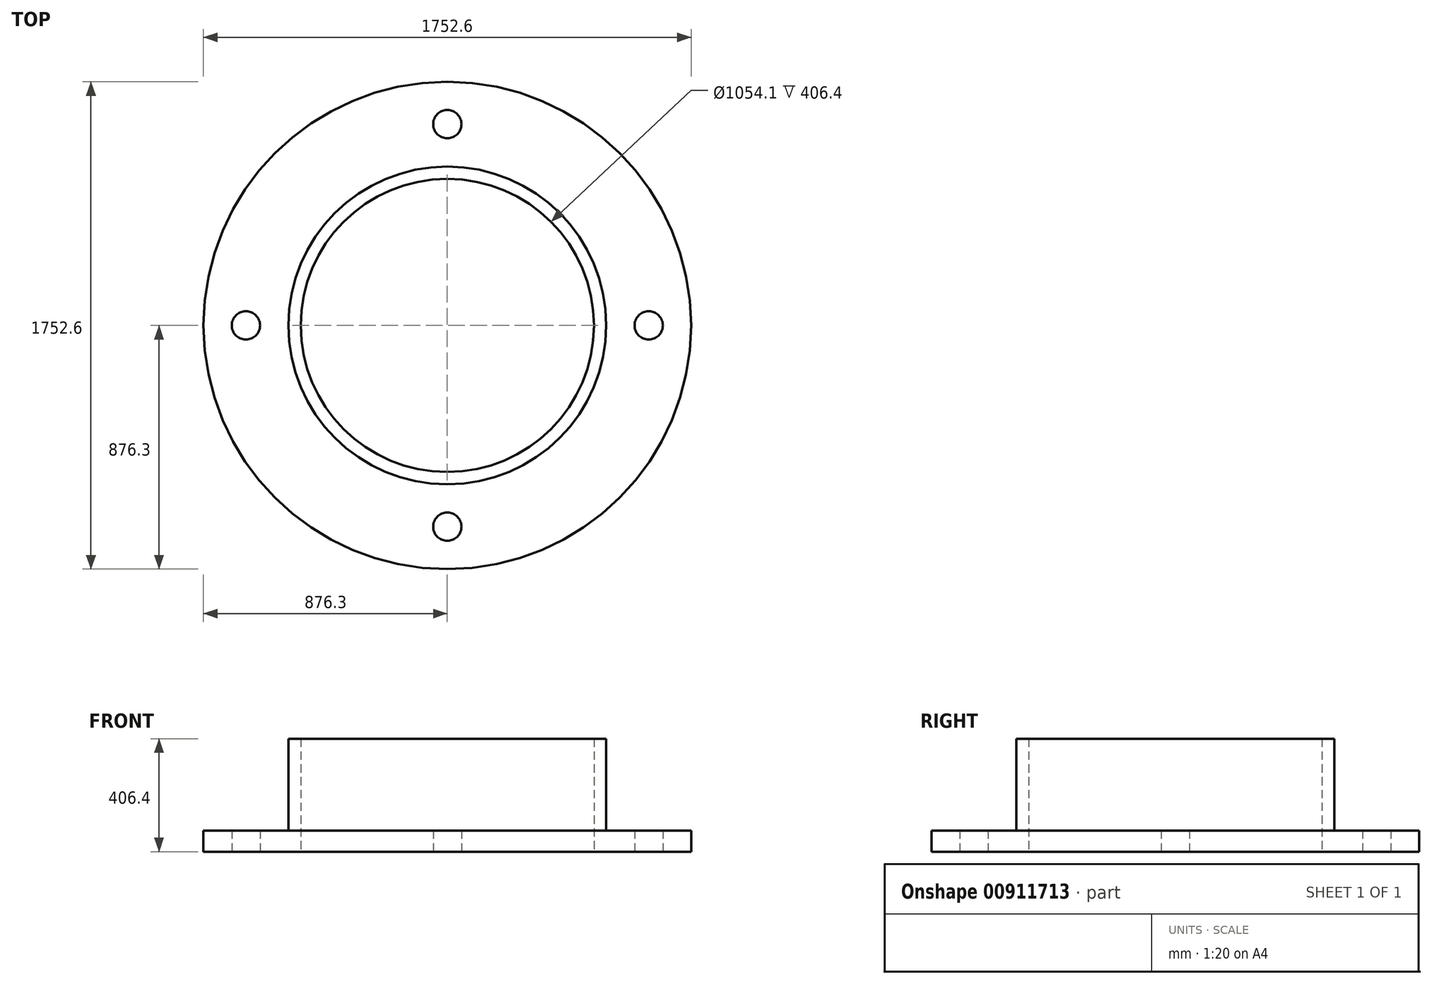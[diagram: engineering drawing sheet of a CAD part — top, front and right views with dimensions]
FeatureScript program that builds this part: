
annotation { "Feature Type Name" : "Feature", "Feature Type Description" : "" }
export const myFeature = defineFeature(function(context is Context, id is Id, definition is map)
    precondition{}
    {
        {
            var Q0;
            Q0=qCreatedBy(makeId("Top.planeOp"),FACE);
            var sketch = newSketch(context, id + "F0", { "sketchPlane" : qUnion([Q0])});
            skPoint(sketch, "E0.middle", {"position": v(0, 0) * mm});
            skCircle(sketch, "E1", {"center": v(0, 0) * mm, "radius": 527.05 * mm});
            skCircle(sketch, "E2", {"center": v(0, 0) * mm, "radius": 571.5 * mm});
            skCircle(sketch, "E3", {"center": v(0, 0) * mm, "radius": 876.3 * mm});
            skCircle(sketch, "E4", {"center": v(0, 723.9) * mm, "radius": 50.8 * mm});
            skCircle(sketch, "E5.1.0", {"center": v(-723.9, 0) * mm, "radius": 50.8 * mm});
            skCircle(sketch, "E5.2.0", {"center": v(0, -723.9) * mm, "radius": 50.8 * mm});
            skCircle(sketch, "E5.3.0", {"center": v(723.9, 0) * mm, "radius": 50.8 * mm});
            skSolve(sketch);
        }
        {
            var Q0;
            {var subQ7=sQuery(id+"F0.wireOp",EDGE,"E0.left");var subQ8=sQuery(id+"F0.wireOp",EDGE,"E0.top");var subQ9=makeQuery(id+"F0.imprint","INTERSECT",VERTEX,{"derivedFrom":[subQ8,subQ7]});Q0=makeQuery(id+"F0.imprint","IMPRINT",FACE,{"disambiguationData":[TD([[makeQuery(id+"F0.imprint","IMPRINT",EDGE,{"disambiguationData":[TD([[subQ9,-1.0]])],"derivedFrom":subQ8}),1.0]])]});}
            var Q1;
            {var subQ0=sQuery(id+"F0.wireOp",EDGE,"bJPlWt6Q-fWFR-6q8K-e8lr-7XfZDWMV1iGK.left");var subQ1=sQuery(id+"F0.wireOp",EDGE,"E0.bottom");var subQ2=makeQuery(id+"F0.imprint","INTERSECT",VERTEX,{"derivedFrom":[subQ1,subQ0]});Q1=makeQuery(id+"F0.imprint","IMPRINT",FACE,{"disambiguationData":[TD([[makeQuery(id+"F0.imprint","IMPRINT",EDGE,{"disambiguationData":[TD([[subQ2,-1.0]])],"derivedFrom":subQ1}),1.0]])]});}
            var Q2;
            {var subQ7=sQuery(id+"F0.wireOp",EDGE,"E0.bottom");var subQ9=sQuery(id+"F0.wireOp",EDGE,"E0.left");var subQ10=makeQuery(id+"F0.imprint","INTERSECT",VERTEX,{"derivedFrom":[subQ7,subQ9]});Q2=makeQuery(id+"F0.imprint","IMPRINT",FACE,{"disambiguationData":[TD([[makeQuery(id+"F0.imprint","IMPRINT",EDGE,{"disambiguationData":[TD([[subQ10,-1.0]])],"derivedFrom":subQ7}),-1.0]])]});}
            var Q3;
            {var subQ0=sQuery(id+"F0.wireOp",EDGE,"bJPlWt6Q-fWFR-6q8K-e8lr-7XfZDWMV1iGK.left");var subQ1=sQuery(id+"F0.wireOp",EDGE,"E0.top");var subQ2=makeQuery(id+"F0.imprint","INTERSECT",VERTEX,{"derivedFrom":[subQ1,subQ0]});Q3=makeQuery(id+"F0.imprint","IMPRINT",FACE,{"disambiguationData":[TD([[makeQuery(id+"F0.imprint","IMPRINT",EDGE,{"disambiguationData":[TD([[subQ2,-1.0]])],"derivedFrom":subQ1}),1.0]])]});}
            var Q4;
            {var subQ0=sQuery(id+"F0.wireOp",EDGE,"bJPlWt6Q-fWFR-6q8K-e8lr-7XfZDWMV1iGK.left");var subQ1=sQuery(id+"F0.wireOp",EDGE,"E0.top");var subQ2=makeQuery(id+"F0.imprint","INTERSECT",VERTEX,{"derivedFrom":[subQ1,subQ0]});Q4=makeQuery(id+"F0.imprint","IMPRINT",FACE,{"disambiguationData":[TD([[makeQuery(id+"F0.imprint","IMPRINT",EDGE,{"disambiguationData":[TD([[subQ2,-1.0]])],"derivedFrom":subQ1}),-1.0]])]});}
            var Q5;
            {var subQ0=sQuery(id+"F0.wireOp",EDGE,"bJPlWt6Q-fWFR-6q8K-e8lr-7XfZDWMV1iGK.left");var subQ1=sQuery(id+"F0.wireOp",EDGE,"E0.bottom");var subQ2=makeQuery(id+"F0.imprint","INTERSECT",VERTEX,{"derivedFrom":[subQ1,subQ0]});Q5=makeQuery(id+"F0.imprint","IMPRINT",FACE,{"disambiguationData":[TD([[makeQuery(id+"F0.imprint","IMPRINT",EDGE,{"disambiguationData":[TD([[subQ2,-1.0]])],"derivedFrom":subQ1}),-1.0]])]});}
            var Q6;
            {var subQ1=sQuery(id+"F0.wireOp",EDGE,"bJPlWt6Q-fWFR-6q8K-e8lr-7XfZDWMV1iGK.bottom");Q6=makeQuery(id+"F0.imprint","IMPRINT",FACE,{"disambiguationData":[TD([[makeQuery(id+"F0.imprint","IMPRINT",EDGE,{"derivedFrom":subQ1}),1.0]])]});}
            var Q7;
            {var subQ0=sQuery(id+"F0.wireOp",EDGE,"uCDm0gm9-0pKr-2IA7-bEzO-ZyxMw17Tw9Nd.bottom");var subQ1=sQuery(id+"F0.wireOp",EDGE,"ElkeHvbq-XJBf-Tpza-nRTL-gXQnVyS3yxsv.left");var subQ2=makeQuery(id+"F0.imprint","INTERSECT",VERTEX,{"derivedFrom":[subQ1,subQ0]});Q7=makeQuery(id+"F0.imprint","IMPRINT",FACE,{"disambiguationData":[TD([[makeQuery(id+"F0.imprint","IMPRINT",EDGE,{"disambiguationData":[TD([[subQ2,-1.0]])],"derivedFrom":subQ1}),1.0]])]});}
            var Q8;
            {var subQ0=sQuery(id+"F0.wireOp",EDGE,"bJPlWt6Q-fWFR-6q8K-e8lr-7XfZDWMV1iGK.right");var subQ1=sQuery(id+"F0.wireOp",EDGE,"E1");var subQ2=makeQuery(id+"F0.imprint","INTERSECT",VERTEX,{"disambiguationData":[OD(1.0)],"derivedFrom":[subQ1,subQ0]});Q8=makeQuery(id+"F0.imprint","IMPRINT",FACE,{"disambiguationData":[TD([[makeQuery(id+"F0.imprint","IMPRINT",EDGE,{"disambiguationData":[TD([[subQ2,-1.0]])],"derivedFrom":subQ1}),-1.0]])]});}
            var Q9;
            {var subQ0=sQuery(id+"F0.wireOp",EDGE,"E0.left");var subQ1=sQuery(id+"F0.wireOp",EDGE,"E0.bottom");var subQ2=makeQuery(id+"F0.imprint","INTERSECT",VERTEX,{"derivedFrom":[subQ1,subQ0]});Q9=makeQuery(id+"F0.imprint","IMPRINT",FACE,{"disambiguationData":[TD([[makeQuery(id+"F0.imprint","IMPRINT",EDGE,{"disambiguationData":[TD([[subQ2,-1.0]])],"derivedFrom":subQ1}),1.0]])]});}
            var Q10;
            {var subQ0=sQuery(id+"F0.wireOp",EDGE,"E0.right");var subQ1=sQuery(id+"F0.wireOp",EDGE,"E0.bottom");var subQ2=makeQuery(id+"F0.imprint","INTERSECT",VERTEX,{"derivedFrom":[subQ1,subQ0]});Q10=makeQuery(id+"F0.imprint","IMPRINT",FACE,{"disambiguationData":[TD([[makeQuery(id+"F0.imprint","IMPRINT",EDGE,{"disambiguationData":[TD([[subQ2,1.0]])],"derivedFrom":subQ1}),1.0]])]});}
            var Q11;
            {var subQ7=sQuery(id+"F0.wireOp",EDGE,"E0.right");var subQ8=sQuery(id+"F0.wireOp",EDGE,"E0.top");var subQ9=makeQuery(id+"F0.imprint","INTERSECT",VERTEX,{"derivedFrom":[subQ8,subQ7]});Q11=makeQuery(id+"F0.imprint","IMPRINT",FACE,{"disambiguationData":[TD([[makeQuery(id+"F0.imprint","IMPRINT",EDGE,{"disambiguationData":[TD([[subQ9,1.0]])],"derivedFrom":subQ8}),1.0]])]});}
            var Q12;
            {var subQ0=sQuery(id+"F0.wireOp",EDGE,"uCDm0gm9-0pKr-2IA7-bEzO-ZyxMw17Tw9Nd.top");var subQ1=sQuery(id+"F0.wireOp",EDGE,"E1");var subQ2=makeQuery(id+"F0.imprint","INTERSECT",VERTEX,{"disambiguationData":[OD(0.0)],"derivedFrom":[subQ1,subQ0]});Q12=makeQuery(id+"F0.imprint","IMPRINT",FACE,{"disambiguationData":[TD([[makeQuery(id+"F0.imprint","IMPRINT",EDGE,{"disambiguationData":[TD([[subQ2,1.0]])],"derivedFrom":subQ1}),-1.0]])]});}
            var Q13;
            {var subQ1=sQuery(id+"F0.wireOp",EDGE,"ElkeHvbq-XJBf-Tpza-nRTL-gXQnVyS3yxsv.bottom");var subQ7=sQuery(id+"F0.wireOp",EDGE,"ElkeHvbq-XJBf-Tpza-nRTL-gXQnVyS3yxsv.right");var subQ9=makeQuery(id+"F0.imprint","INTERSECT",VERTEX,{"derivedFrom":[subQ1,subQ7]});Q13=makeQuery(id+"F0.imprint","IMPRINT",FACE,{"disambiguationData":[TD([[makeQuery(id+"F0.imprint","IMPRINT",EDGE,{"disambiguationData":[TD([[subQ9,1.0]])],"derivedFrom":subQ1}),-1.0]])]});}
            var Q14;
            {var subQ0=sQuery(id+"F0.wireOp",EDGE,"uCDm0gm9-0pKr-2IA7-bEzO-ZyxMw17Tw9Nd.bottom");var subQ1=sQuery(id+"F0.wireOp",EDGE,"E0.left");var subQ2=makeQuery(id+"F0.imprint","INTERSECT",VERTEX,{"derivedFrom":[subQ1,subQ0]});Q14=makeQuery(id+"F0.imprint","IMPRINT",FACE,{"disambiguationData":[TD([[makeQuery(id+"F0.imprint","IMPRINT",EDGE,{"disambiguationData":[TD([[subQ2,-1.0]])],"derivedFrom":subQ1}),1.0]])]});}
            var Q15;
            {var subQ0=sQuery(id+"F0.wireOp",EDGE,"E0.right");var subQ1=sQuery(id+"F0.wireOp",EDGE,"E0.top");var subQ2=makeQuery(id+"F0.imprint","INTERSECT",VERTEX,{"derivedFrom":[subQ1,subQ0]});Q15=makeQuery(id+"F0.imprint","IMPRINT",FACE,{"disambiguationData":[TD([[makeQuery(id+"F0.imprint","IMPRINT",EDGE,{"disambiguationData":[TD([[subQ2,1.0]])],"derivedFrom":subQ1}),-1.0]])]});}
            var Q16;
            {var subQ0=sQuery(id+"F0.wireOp",EDGE,"uCDm0gm9-0pKr-2IA7-bEzO-ZyxMw17Tw9Nd.bottom");var subQ1=sQuery(id+"F0.wireOp",EDGE,"E0.right");var subQ2=makeQuery(id+"F0.imprint","INTERSECT",VERTEX,{"derivedFrom":[subQ1,subQ0]});Q16=makeQuery(id+"F0.imprint","IMPRINT",FACE,{"disambiguationData":[TD([[makeQuery(id+"F0.imprint","IMPRINT",EDGE,{"disambiguationData":[TD([[subQ2,-1.0]])],"derivedFrom":subQ1}),-1.0]])]});}
            var Q17;
            {var subQ0=sQuery(id+"F0.wireOp",EDGE,"bJPlWt6Q-fWFR-6q8K-e8lr-7XfZDWMV1iGK.left");var subQ1=sQuery(id+"F0.wireOp",EDGE,"E1");var subQ2=makeQuery(id+"F0.imprint","INTERSECT",VERTEX,{"disambiguationData":[OD(1.0)],"derivedFrom":[subQ1,subQ0]});Q17=makeQuery(id+"F0.imprint","IMPRINT",FACE,{"disambiguationData":[TD([[makeQuery(id+"F0.imprint","IMPRINT",EDGE,{"disambiguationData":[TD([[subQ2,-1.0]])],"derivedFrom":subQ1}),-1.0]])]});}
            var Q18;
            {var subQ1=sQuery(id+"F0.wireOp",EDGE,"ElkeHvbq-XJBf-Tpza-nRTL-gXQnVyS3yxsv.top");var subQ5=sQuery(id+"F0.wireOp",EDGE,"ElkeHvbq-XJBf-Tpza-nRTL-gXQnVyS3yxsv.right");var subQ6=makeQuery(id+"F0.imprint","INTERSECT",VERTEX,{"derivedFrom":[subQ1,subQ5]});Q18=makeQuery(id+"F0.imprint","IMPRINT",FACE,{"disambiguationData":[TD([[makeQuery(id+"F0.imprint","IMPRINT",EDGE,{"disambiguationData":[TD([[subQ6,1.0]])],"derivedFrom":subQ1}),1.0]])]});}
            var Q19;
            {var subQ0=sQuery(id+"F0.wireOp",EDGE,"uCDm0gm9-0pKr-2IA7-bEzO-ZyxMw17Tw9Nd.top");var subQ1=sQuery(id+"F0.wireOp",EDGE,"E1");var subQ2=makeQuery(id+"F0.imprint","INTERSECT",VERTEX,{"disambiguationData":[OD(1.0)],"derivedFrom":[subQ1,subQ0]});Q19=makeQuery(id+"F0.imprint","IMPRINT",FACE,{"disambiguationData":[TD([[makeQuery(id+"F0.imprint","IMPRINT",EDGE,{"disambiguationData":[TD([[subQ2,-1.0]])],"derivedFrom":subQ1}),-1.0]])]});}
            var Q20;
            {var subQ0=sQuery(id+"F0.wireOp",EDGE,"uCDm0gm9-0pKr-2IA7-bEzO-ZyxMw17Tw9Nd.bottom");var subQ1=sQuery(id+"F0.wireOp",EDGE,"ElkeHvbq-XJBf-Tpza-nRTL-gXQnVyS3yxsv.right");var subQ2=makeQuery(id+"F0.imprint","INTERSECT",VERTEX,{"derivedFrom":[subQ1,subQ0]});Q20=makeQuery(id+"F0.imprint","IMPRINT",FACE,{"disambiguationData":[TD([[makeQuery(id+"F0.imprint","IMPRINT",EDGE,{"disambiguationData":[TD([[subQ2,-1.0]])],"derivedFrom":subQ1}),-1.0]])]});}
            var Q21;
            {var subQ0=sQuery(id+"F0.wireOp",EDGE,"uCDm0gm9-0pKr-2IA7-bEzO-ZyxMw17Tw9Nd.right");Q21=makeQuery(id+"F0.imprint","IMPRINT",FACE,{"disambiguationData":[TD([[makeQuery(id+"F0.imprint","IMPRINT",EDGE,{"derivedFrom":subQ0}),1.0]])]});}
            var Q22;
            {var subQ0=sQuery(id+"F0.wireOp",EDGE,"E0.left");var subQ1=sQuery(id+"F0.wireOp",EDGE,"E0.top");var subQ2=makeQuery(id+"F0.imprint","INTERSECT",VERTEX,{"derivedFrom":[subQ1,subQ0]});Q22=makeQuery(id+"F0.imprint","IMPRINT",FACE,{"disambiguationData":[TD([[makeQuery(id+"F0.imprint","IMPRINT",EDGE,{"disambiguationData":[TD([[subQ2,-1.0]])],"derivedFrom":subQ1}),-1.0]])]});}
            var Q23;
            {var subQ0=sQuery(id+"F0.wireOp",EDGE,"uCDm0gm9-0pKr-2IA7-bEzO-ZyxMw17Tw9Nd.bottom");var subQ1=sQuery(id+"F0.wireOp",EDGE,"E0.right");var subQ2=makeQuery(id+"F0.imprint","INTERSECT",VERTEX,{"derivedFrom":[subQ1,subQ0]});Q23=makeQuery(id+"F0.imprint","IMPRINT",FACE,{"disambiguationData":[TD([[makeQuery(id+"F0.imprint","IMPRINT",EDGE,{"disambiguationData":[TD([[subQ2,-1.0]])],"derivedFrom":subQ1}),1.0]])]});}
            var Q24;
            {var subQ0=sQuery(id+"F0.wireOp",EDGE,"uCDm0gm9-0pKr-2IA7-bEzO-ZyxMw17Tw9Nd.bottom");var subQ1=sQuery(id+"F0.wireOp",EDGE,"E1");var subQ2=makeQuery(id+"F0.imprint","INTERSECT",VERTEX,{"disambiguationData":[OD(0.0)],"derivedFrom":[subQ1,subQ0]});Q24=makeQuery(id+"F0.imprint","IMPRINT",FACE,{"disambiguationData":[TD([[makeQuery(id+"F0.imprint","IMPRINT",EDGE,{"disambiguationData":[TD([[subQ2,-1.0]])],"derivedFrom":subQ1}),-1.0]])]});}
            var Q25;
            {var subQ0=sQuery(id+"F0.wireOp",EDGE,"uCDm0gm9-0pKr-2IA7-bEzO-ZyxMw17Tw9Nd.bottom");var subQ1=sQuery(id+"F0.wireOp",EDGE,"E0.left");var subQ2=makeQuery(id+"F0.imprint","INTERSECT",VERTEX,{"derivedFrom":[subQ1,subQ0]});Q25=makeQuery(id+"F0.imprint","IMPRINT",FACE,{"disambiguationData":[TD([[makeQuery(id+"F0.imprint","IMPRINT",EDGE,{"disambiguationData":[TD([[subQ2,-1.0]])],"derivedFrom":subQ1}),-1.0]])]});}
            var Q26;
            {var subQ0=sQuery(id+"F0.wireOp",EDGE,"bJPlWt6Q-fWFR-6q8K-e8lr-7XfZDWMV1iGK.left");var subQ1=sQuery(id+"F0.wireOp",EDGE,"ElkeHvbq-XJBf-Tpza-nRTL-gXQnVyS3yxsv.bottom");var subQ2=makeQuery(id+"F0.imprint","INTERSECT",VERTEX,{"derivedFrom":[subQ1,subQ0]});Q26=makeQuery(id+"F0.imprint","IMPRINT",FACE,{"disambiguationData":[TD([[makeQuery(id+"F0.imprint","IMPRINT",EDGE,{"disambiguationData":[TD([[subQ2,-1.0]])],"derivedFrom":subQ1}),-1.0]])]});}
            var Q27;
            {var subQ0=sQuery(id+"F0.wireOp",EDGE,"uCDm0gm9-0pKr-2IA7-bEzO-ZyxMw17Tw9Nd.left");Q27=makeQuery(id+"F0.imprint","IMPRINT",FACE,{"disambiguationData":[TD([[makeQuery(id+"F0.imprint","IMPRINT",EDGE,{"derivedFrom":subQ0}),-1.0]])]});}
            var Q28;
            {var subQ1=sQuery(id+"F0.wireOp",EDGE,"bJPlWt6Q-fWFR-6q8K-e8lr-7XfZDWMV1iGK.top");Q28=makeQuery(id+"F0.imprint","IMPRINT",FACE,{"disambiguationData":[TD([[makeQuery(id+"F0.imprint","IMPRINT",EDGE,{"derivedFrom":subQ1}),-1.0]])]});}
            var Q29;
            {var subQ0=sQuery(id+"F0.wireOp",EDGE,"bJPlWt6Q-fWFR-6q8K-e8lr-7XfZDWMV1iGK.left");var subQ1=sQuery(id+"F0.wireOp",EDGE,"ElkeHvbq-XJBf-Tpza-nRTL-gXQnVyS3yxsv.top");var subQ2=makeQuery(id+"F0.imprint","INTERSECT",VERTEX,{"derivedFrom":[subQ1,subQ0]});Q29=makeQuery(id+"F0.imprint","IMPRINT",FACE,{"disambiguationData":[TD([[makeQuery(id+"F0.imprint","IMPRINT",EDGE,{"disambiguationData":[TD([[subQ2,-1.0]])],"derivedFrom":subQ1}),1.0]])]});}
            var Q30;
            {var subQ0=sQuery(id+"F0.wireOp",EDGE,"bJPlWt6Q-fWFR-6q8K-e8lr-7XfZDWMV1iGK.right");var subQ1=sQuery(id+"F0.wireOp",EDGE,"E1");var subQ2=makeQuery(id+"F0.imprint","INTERSECT",VERTEX,{"disambiguationData":[OD(0.0)],"derivedFrom":[subQ1,subQ0]});Q30=makeQuery(id+"F0.imprint","IMPRINT",FACE,{"disambiguationData":[TD([[makeQuery(id+"F0.imprint","IMPRINT",EDGE,{"disambiguationData":[TD([[subQ2,-1.0]])],"derivedFrom":subQ1}),-1.0]])]});}
            var Q31;
            {var subQ0=sQuery(id+"F0.wireOp",EDGE,"bJPlWt6Q-fWFR-6q8K-e8lr-7XfZDWMV1iGK.right");var subQ1=sQuery(id+"F0.wireOp",EDGE,"E1");var subQ2=makeQuery(id+"F0.imprint","INTERSECT",VERTEX,{"disambiguationData":[OD(0.0)],"derivedFrom":[subQ1,subQ0]});Q31=makeQuery(id+"F0.imprint","IMPRINT",FACE,{"disambiguationData":[TD([[makeQuery(id+"F0.imprint","IMPRINT",EDGE,{"disambiguationData":[TD([[subQ2,1.0]])],"derivedFrom":subQ1}),-1.0]])]});}
            var Q32;
            {var subQ0=sQuery(id+"F0.wireOp",EDGE,"bJPlWt6Q-fWFR-6q8K-e8lr-7XfZDWMV1iGK.left");var subQ1=sQuery(id+"F0.wireOp",EDGE,"E1");var subQ2=makeQuery(id+"F0.imprint","INTERSECT",VERTEX,{"disambiguationData":[OD(0.0)],"derivedFrom":[subQ1,subQ0]});Q32=makeQuery(id+"F0.imprint","IMPRINT",FACE,{"disambiguationData":[TD([[makeQuery(id+"F0.imprint","IMPRINT",EDGE,{"disambiguationData":[TD([[subQ2,-1.0]])],"derivedFrom":subQ1}),-1.0]])]});}
            var Q33;
            {var subQ5=sQuery(id+"F0.wireOp",EDGE,"ElkeHvbq-XJBf-Tpza-nRTL-gXQnVyS3yxsv.left");var subQ6=sQuery(id+"F0.wireOp",EDGE,"ElkeHvbq-XJBf-Tpza-nRTL-gXQnVyS3yxsv.top");var subQ7=makeQuery(id+"F0.imprint","INTERSECT",VERTEX,{"derivedFrom":[subQ6,subQ5]});Q33=makeQuery(id+"F0.imprint","IMPRINT",FACE,{"disambiguationData":[TD([[makeQuery(id+"F0.imprint","IMPRINT",EDGE,{"disambiguationData":[TD([[subQ7,-1.0]])],"derivedFrom":subQ6}),1.0]])]});}
            var Q34;
            {var subQ1=sQuery(id+"F0.wireOp",EDGE,"ElkeHvbq-XJBf-Tpza-nRTL-gXQnVyS3yxsv.bottom");var subQ5=sQuery(id+"F0.wireOp",EDGE,"ElkeHvbq-XJBf-Tpza-nRTL-gXQnVyS3yxsv.right");var subQ6=makeQuery(id+"F0.imprint","INTERSECT",VERTEX,{"derivedFrom":[subQ1,subQ5]});Q34=makeQuery(id+"F0.imprint","IMPRINT",FACE,{"disambiguationData":[TD([[makeQuery(id+"F0.imprint","IMPRINT",EDGE,{"disambiguationData":[TD([[subQ6,1.0]])],"derivedFrom":subQ1}),1.0]])]});}
            var Q35;
            {var subQ1=sQuery(id+"F0.wireOp",EDGE,"E0.right");var subQ9=sQuery(id+"F0.wireOp",EDGE,"E0.bottom");var subQ11=makeQuery(id+"F0.imprint","INTERSECT",VERTEX,{"derivedFrom":[subQ9,subQ1]});Q35=makeQuery(id+"F0.imprint","IMPRINT",FACE,{"disambiguationData":[TD([[makeQuery(id+"F0.imprint","IMPRINT",EDGE,{"disambiguationData":[TD([[subQ11,1.0]])],"derivedFrom":subQ9}),-1.0]])]});}
            var Q36;
            {var subQ0=sQuery(id+"F0.wireOp",EDGE,"bJPlWt6Q-fWFR-6q8K-e8lr-7XfZDWMV1iGK.left");var subQ1=sQuery(id+"F0.wireOp",EDGE,"ElkeHvbq-XJBf-Tpza-nRTL-gXQnVyS3yxsv.bottom");var subQ2=makeQuery(id+"F0.imprint","INTERSECT",VERTEX,{"derivedFrom":[subQ1,subQ0]});Q36=makeQuery(id+"F0.imprint","IMPRINT",FACE,{"disambiguationData":[TD([[makeQuery(id+"F0.imprint","IMPRINT",EDGE,{"disambiguationData":[TD([[subQ2,-1.0]])],"derivedFrom":subQ1}),1.0]])]});}
            var Q37;
            {var subQ0=sQuery(id+"F0.wireOp",EDGE,"uCDm0gm9-0pKr-2IA7-bEzO-ZyxMw17Tw9Nd.bottom");var subQ1=sQuery(id+"F0.wireOp",EDGE,"ElkeHvbq-XJBf-Tpza-nRTL-gXQnVyS3yxsv.left");var subQ2=makeQuery(id+"F0.imprint","INTERSECT",VERTEX,{"derivedFrom":[subQ1,subQ0]});Q37=makeQuery(id+"F0.imprint","IMPRINT",FACE,{"disambiguationData":[TD([[makeQuery(id+"F0.imprint","IMPRINT",EDGE,{"disambiguationData":[TD([[subQ2,-1.0]])],"derivedFrom":subQ1}),-1.0]])]});}
            var Q38;
            {var subQ1=sQuery(id+"F0.wireOp",EDGE,"ElkeHvbq-XJBf-Tpza-nRTL-gXQnVyS3yxsv.left");var subQ5=sQuery(id+"F0.wireOp",EDGE,"ElkeHvbq-XJBf-Tpza-nRTL-gXQnVyS3yxsv.top");var subQ6=makeQuery(id+"F0.imprint","INTERSECT",VERTEX,{"derivedFrom":[subQ5,subQ1]});Q38=makeQuery(id+"F0.imprint","IMPRINT",FACE,{"disambiguationData":[TD([[makeQuery(id+"F0.imprint","IMPRINT",EDGE,{"disambiguationData":[TD([[subQ6,-1.0]])],"derivedFrom":subQ5}),-1.0]])]});}
            var Q39;
            {var subQ0=sQuery(id+"F0.wireOp",EDGE,"uCDm0gm9-0pKr-2IA7-bEzO-ZyxMw17Tw9Nd.bottom");var subQ1=sQuery(id+"F0.wireOp",EDGE,"ElkeHvbq-XJBf-Tpza-nRTL-gXQnVyS3yxsv.right");var subQ2=makeQuery(id+"F0.imprint","INTERSECT",VERTEX,{"derivedFrom":[subQ1,subQ0]});Q39=makeQuery(id+"F0.imprint","IMPRINT",FACE,{"disambiguationData":[TD([[makeQuery(id+"F0.imprint","IMPRINT",EDGE,{"disambiguationData":[TD([[subQ2,-1.0]])],"derivedFrom":subQ1}),1.0]])]});}
            var Q40;
            {var subQ1=sQuery(id+"F0.wireOp",EDGE,"ElkeHvbq-XJBf-Tpza-nRTL-gXQnVyS3yxsv.bottom");var subQ7=sQuery(id+"F0.wireOp",EDGE,"ElkeHvbq-XJBf-Tpza-nRTL-gXQnVyS3yxsv.left");var subQ9=makeQuery(id+"F0.imprint","INTERSECT",VERTEX,{"derivedFrom":[subQ1,subQ7]});Q40=makeQuery(id+"F0.imprint","IMPRINT",FACE,{"disambiguationData":[TD([[makeQuery(id+"F0.imprint","IMPRINT",EDGE,{"disambiguationData":[TD([[subQ9,-1.0]])],"derivedFrom":subQ1}),-1.0]])]});}
            var Q41;
            {var subQ0=sQuery(id+"F0.wireOp",EDGE,"bJPlWt6Q-fWFR-6q8K-e8lr-7XfZDWMV1iGK.left");var subQ1=sQuery(id+"F0.wireOp",EDGE,"ElkeHvbq-XJBf-Tpza-nRTL-gXQnVyS3yxsv.top");var subQ2=makeQuery(id+"F0.imprint","INTERSECT",VERTEX,{"derivedFrom":[subQ1,subQ0]});Q41=makeQuery(id+"F0.imprint","IMPRINT",FACE,{"disambiguationData":[TD([[makeQuery(id+"F0.imprint","IMPRINT",EDGE,{"disambiguationData":[TD([[subQ2,-1.0]])],"derivedFrom":subQ1}),-1.0]])]});}
            var Q42;
            {var subQ1=sQuery(id+"F0.wireOp",EDGE,"ElkeHvbq-XJBf-Tpza-nRTL-gXQnVyS3yxsv.bottom");var subQ5=sQuery(id+"F0.wireOp",EDGE,"ElkeHvbq-XJBf-Tpza-nRTL-gXQnVyS3yxsv.left");var subQ6=makeQuery(id+"F0.imprint","INTERSECT",VERTEX,{"derivedFrom":[subQ1,subQ5]});Q42=makeQuery(id+"F0.imprint","IMPRINT",FACE,{"disambiguationData":[TD([[makeQuery(id+"F0.imprint","IMPRINT",EDGE,{"disambiguationData":[TD([[subQ6,-1.0]])],"derivedFrom":subQ1}),1.0]])]});}
            var Q43;
            {var subQ1=sQuery(id+"F0.wireOp",EDGE,"ElkeHvbq-XJBf-Tpza-nRTL-gXQnVyS3yxsv.top");var subQ9=sQuery(id+"F0.wireOp",EDGE,"ElkeHvbq-XJBf-Tpza-nRTL-gXQnVyS3yxsv.right");var subQ10=makeQuery(id+"F0.imprint","INTERSECT",VERTEX,{"derivedFrom":[subQ1,subQ9]});Q43=makeQuery(id+"F0.imprint","IMPRINT",FACE,{"disambiguationData":[TD([[makeQuery(id+"F0.imprint","IMPRINT",EDGE,{"disambiguationData":[TD([[subQ10,1.0]])],"derivedFrom":subQ1}),-1.0]])]});}
            var Q44;
            Q44=makeQuery(id+"F0.imprint","IMPRINT",FACE,{"disambiguationData":[TD([[makeQuery(id+"F0.imprint","IMPRINT",EDGE,{"derivedFrom":sQuery(id+"F0.wireOp",EDGE,"fNri1SRu-FuhW-Q3Wo-20dk-0Yi258a3IsZ0")}),-1.0]])]});
            var Q45;
            {var subQ4=sQuery(id+"F0.wireOp",EDGE,"VQf29DOb-Ug8P-LxES-Ujji-pntrdd86x7RR.top");var subQ5=sQuery(id+"F0.wireOp",EDGE,"E2");var subQ6=makeQuery(id+"F0.imprint","INTERSECT",VERTEX,{"derivedFrom":[subQ5,subQ4]});Q45=makeQuery(id+"F0.imprint","IMPRINT",FACE,{"disambiguationData":[TD([[makeQuery(id+"F0.imprint","IMPRINT",EDGE,{"disambiguationData":[TD([[subQ6,-1.0]])],"derivedFrom":subQ5}),1.0]])]});}
            var Q46;
            Q46=makeQuery(id+"F0.imprint","IMPRINT",FACE,{"disambiguationData":[TD([[makeQuery(id+"F0.imprint","IMPRINT",EDGE,{"derivedFrom":sQuery(id+"F0.wireOp",EDGE,"70675ac1-52d6-47e0-aa64-0ae3552453f1.3.1")}),-1.0]])]});
            var Q47;
            {var subQ0=sQuery(id+"F0.wireOp",EDGE,"70675ac1-52d6-47e0-aa64-0ae3552453f1.3.2");var subQ6=sQuery(id+"F0.wireOp",EDGE,"E2");var subQ7=makeQuery(id+"F0.imprint","INTERSECT",VERTEX,{"derivedFrom":[subQ6,subQ0]});Q47=makeQuery(id+"F0.imprint","IMPRINT",FACE,{"disambiguationData":[TD([[makeQuery(id+"F0.imprint","IMPRINT",EDGE,{"disambiguationData":[TD([[subQ7,-1.0]])],"derivedFrom":subQ6}),1.0]])]});}
            var Q48;
            Q48=makeQuery(id+"F0.imprint","IMPRINT",FACE,{"disambiguationData":[TD([[makeQuery(id+"F0.imprint","IMPRINT",EDGE,{"derivedFrom":sQuery(id+"F0.wireOp",EDGE,"70675ac1-52d6-47e0-aa64-0ae3552453f1.2.1")}),-1.0]])]});
            var Q49;
            {var subQ3=sQuery(id+"F0.wireOp",EDGE,"E2");var subQ6=sQuery(id+"F0.wireOp",EDGE,"70675ac1-52d6-47e0-aa64-0ae3552453f1.2.4");var subQ8=makeQuery(id+"F0.imprint","INTERSECT",VERTEX,{"derivedFrom":[subQ3,subQ6]});Q49=makeQuery(id+"F0.imprint","IMPRINT",FACE,{"disambiguationData":[TD([[makeQuery(id+"F0.imprint","IMPRINT",EDGE,{"disambiguationData":[TD([[subQ8,1.0]])],"derivedFrom":subQ3}),1.0]])]});}
            var Q50;
            Q50=makeQuery(id+"F0.imprint","IMPRINT",FACE,{"disambiguationData":[TD([[makeQuery(id+"F0.imprint","IMPRINT",EDGE,{"derivedFrom":sQuery(id+"F0.wireOp",EDGE,"70675ac1-52d6-47e0-aa64-0ae3552453f1.1.1")}),-1.0]])]});
            var Q51;
            {var subQ0=sQuery(id+"F0.wireOp",EDGE,"70675ac1-52d6-47e0-aa64-0ae3552453f1.1.2");var subQ6=sQuery(id+"F0.wireOp",EDGE,"E2");var subQ7=makeQuery(id+"F0.imprint","INTERSECT",VERTEX,{"derivedFrom":[subQ6,subQ0]});Q51=makeQuery(id+"F0.imprint","IMPRINT",FACE,{"disambiguationData":[TD([[makeQuery(id+"F0.imprint","IMPRINT",EDGE,{"disambiguationData":[TD([[subQ7,-1.0]])],"derivedFrom":subQ6}),1.0]])]});}
            var Q52;
            Q52=makeQuery(id+"F0.imprint","IMPRINT",FACE,{"disambiguationData":[TD([[makeQuery(id+"F0.imprint","IMPRINT",EDGE,{"derivedFrom":sQuery(id+"F0.wireOp",EDGE,"E2")}),-1.0]])]});
            extrude(context, id + "F1", {"entities" : qUnion([Q0, Q1, Q2, Q3, Q4, Q5, Q6, Q7, Q8, Q9, Q10, Q11, Q12, Q13, Q14, Q15, Q16, Q17, Q18, Q19, Q20, Q21, Q22, Q23, Q24, Q25, Q26, Q27, Q28, Q29, Q30, Q31, Q32, Q33, Q34, Q35, Q36, Q37, Q38, Q39, Q40, Q41, Q42, Q43, Q44, Q45, Q46, Q47, Q48, Q49, Q50, Q51, Q52]), "depth" : 76.2 * mm, "offsetDistance" : 25.4 * mm});
        }
        {
            var Q0;
            {var subQ4=sQuery(id+"F0.wireOp",EDGE,"VQf29DOb-Ug8P-LxES-Ujji-pntrdd86x7RR.top");var subQ5=sQuery(id+"F0.wireOp",EDGE,"E2");var subQ6=makeQuery(id+"F0.imprint","INTERSECT",VERTEX,{"derivedFrom":[subQ5,subQ4]});Q0=makeQuery(id+"F0.imprint","IMPRINT",FACE,{"disambiguationData":[TD([[makeQuery(id+"F0.imprint","IMPRINT",EDGE,{"disambiguationData":[TD([[subQ6,-1.0]])],"derivedFrom":subQ5}),1.0]])]});}
            var Q1;
            {var subQ0=sQuery(id+"F0.wireOp",EDGE,"VQf29DOb-Ug8P-LxES-Ujji-pntrdd86x7RR.right");var subQ5=sQuery(id+"F0.wireOp",EDGE,"E1");var subQ6=makeQuery(id+"F0.imprint","INTERSECT",VERTEX,{"derivedFrom":[subQ5,subQ0]});Q1=makeQuery(id+"F0.imprint","IMPRINT",FACE,{"disambiguationData":[TD([[makeQuery(id+"F0.imprint","IMPRINT",EDGE,{"disambiguationData":[TD([[subQ6,-1.0]])],"derivedFrom":subQ5}),-1.0]])]});}
            var Q2;
            {var subQ0=sQuery(id+"F0.wireOp",EDGE,"70675ac1-52d6-47e0-aa64-0ae3552453f1.1.2");var subQ6=sQuery(id+"F0.wireOp",EDGE,"E2");var subQ7=makeQuery(id+"F0.imprint","INTERSECT",VERTEX,{"derivedFrom":[subQ6,subQ0]});Q2=makeQuery(id+"F0.imprint","IMPRINT",FACE,{"disambiguationData":[TD([[makeQuery(id+"F0.imprint","IMPRINT",EDGE,{"disambiguationData":[TD([[subQ7,-1.0]])],"derivedFrom":subQ6}),1.0]])]});}
            var Q3;
            {var subQ5=sQuery(id+"F0.wireOp",EDGE,"E1");var subQ9=sQuery(id+"F0.wireOp",EDGE,"70675ac1-52d6-47e0-aa64-0ae3552453f1.2.0");var subQ11=makeQuery(id+"F0.imprint","INTERSECT",VERTEX,{"derivedFrom":[subQ5,subQ9]});Q3=makeQuery(id+"F0.imprint","IMPRINT",FACE,{"disambiguationData":[TD([[makeQuery(id+"F0.imprint","IMPRINT",EDGE,{"disambiguationData":[TD([[subQ11,1.0]])],"derivedFrom":subQ5}),-1.0]])]});}
            var Q4;
            {var subQ3=sQuery(id+"F0.wireOp",EDGE,"E2");var subQ6=sQuery(id+"F0.wireOp",EDGE,"70675ac1-52d6-47e0-aa64-0ae3552453f1.2.4");var subQ8=makeQuery(id+"F0.imprint","INTERSECT",VERTEX,{"derivedFrom":[subQ3,subQ6]});Q4=makeQuery(id+"F0.imprint","IMPRINT",FACE,{"disambiguationData":[TD([[makeQuery(id+"F0.imprint","IMPRINT",EDGE,{"disambiguationData":[TD([[subQ8,1.0]])],"derivedFrom":subQ3}),1.0]])]});}
            var Q5;
            {var subQ3=sQuery(id+"F0.wireOp",EDGE,"E1");var subQ9=sQuery(id+"F0.wireOp",EDGE,"70675ac1-52d6-47e0-aa64-0ae3552453f1.3.0");var subQ11=makeQuery(id+"F0.imprint","INTERSECT",VERTEX,{"derivedFrom":[subQ3,subQ9]});Q5=makeQuery(id+"F0.imprint","IMPRINT",FACE,{"disambiguationData":[TD([[makeQuery(id+"F0.imprint","IMPRINT",EDGE,{"disambiguationData":[TD([[subQ11,1.0]])],"derivedFrom":subQ3}),-1.0]])]});}
            var Q6;
            {var subQ3=sQuery(id+"F0.wireOp",EDGE,"E1");var subQ9=sQuery(id+"F0.wireOp",EDGE,"70675ac1-52d6-47e0-aa64-0ae3552453f1.3.0");var subQ10=makeQuery(id+"F0.imprint","INTERSECT",VERTEX,{"derivedFrom":[subQ3,subQ9]});Q6=makeQuery(id+"F0.imprint","IMPRINT",FACE,{"disambiguationData":[TD([[makeQuery(id+"F0.imprint","IMPRINT",EDGE,{"disambiguationData":[TD([[subQ10,-1.0]])],"derivedFrom":subQ3}),-1.0]])]});}
            var Q7;
            {var subQ0=sQuery(id+"F0.wireOp",EDGE,"70675ac1-52d6-47e0-aa64-0ae3552453f1.3.2");var subQ6=sQuery(id+"F0.wireOp",EDGE,"E2");var subQ7=makeQuery(id+"F0.imprint","INTERSECT",VERTEX,{"derivedFrom":[subQ6,subQ0]});Q7=makeQuery(id+"F0.imprint","IMPRINT",FACE,{"disambiguationData":[TD([[makeQuery(id+"F0.imprint","IMPRINT",EDGE,{"disambiguationData":[TD([[subQ7,-1.0]])],"derivedFrom":subQ6}),1.0]])]});}
            extrude(context, id + "F2", {"entities" : qUnion([Q0, Q1, Q2, Q3, Q4, Q5, Q6, Q7]), "operationType" : NewBodyOperationType.ADD, "depth" : 406.4 * mm, "offsetDistance" : 25.4 * mm});
        }
    });
